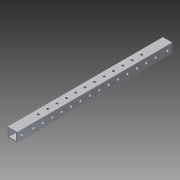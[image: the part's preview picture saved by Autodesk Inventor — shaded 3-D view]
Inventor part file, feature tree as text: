
AUTODESK INVENTOR PART (.ipt)
format: ipt  version: 2013 (Build 170138000, 138)  size: 169,984 bytes
history: native  units: in
note: dims shown in document units (in); Inventor stores cm internally (conversion verified against a paired STEP export)
features: extrude x3, sketch x3
ambient origin geometry x8: Origin, YZ Plane, XZ Plane, XY Plane, X Axis, Y Axis, Z Axis, Center Point
bodies: Solid1 (feature_tree)
feature tree (6):
  extrude  "Extrusion1"  Depth=1.0in
  extrude  "Extrusion2"  Depth=16.5in TaperAngle=0.0deg
  extrude  "Extrusion3"  Depth=0.26in
  sketch  "Sketch1"  dims[d0=1.0in d1=1.0in]
  sketch  "Sketch2"  dims[d2=0.125in d3=16.5in d4=0.0in]
  sketch  "Sketch3"  dims[d5=0.75in d7=0.26in d8=16.5in d9=0.0in d10=16.5in d11=6.2992in d13=1.0in d14=0.3937in d16=1.0in d18=0.75in d19=0.5in d20=0.26in d21=0.26in d22=0.5in d23=0.26in d25=0.75in d26=6.2992in d28=1.0in d29=0.3937in d31=1.0in d33=0.75in d34=1.0in d35=0.0in]
